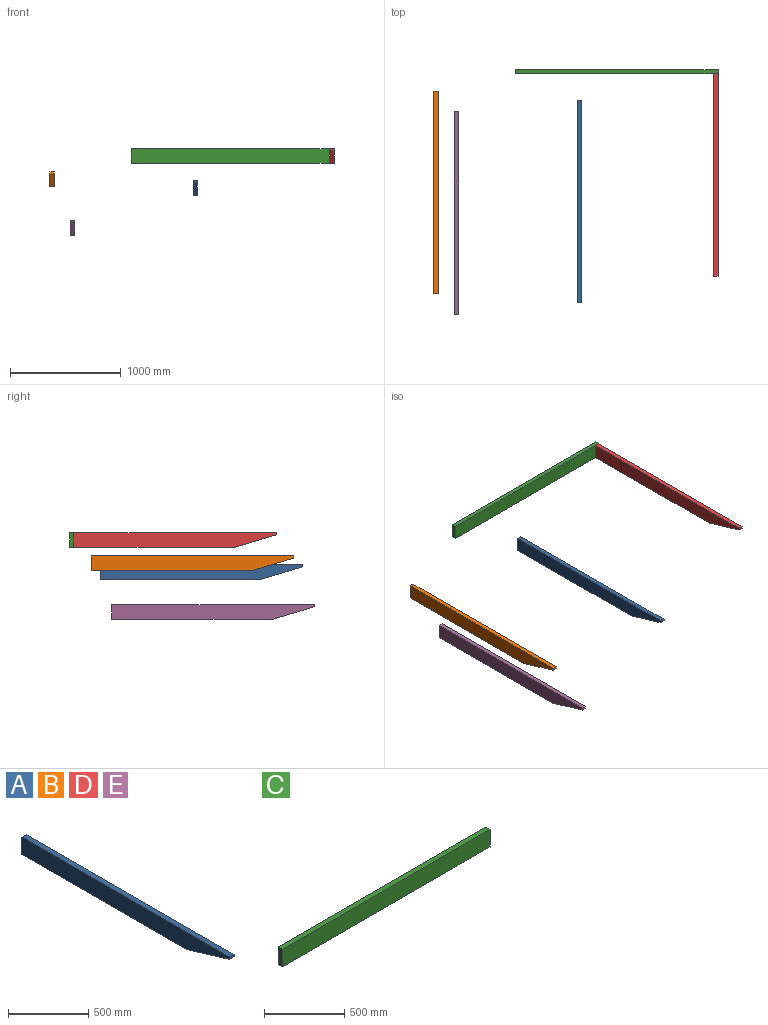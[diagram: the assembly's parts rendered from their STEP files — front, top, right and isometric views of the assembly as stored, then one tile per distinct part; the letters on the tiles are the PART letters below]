
ASSEMBLY  parts=5 mates=1
PART A: 7 faces, bbox 38.1x1828.8x133.4 mm
  f0: plane 1447.8x38.1mm, normal (0,0,-1), area 55161.2mm2, adj f2,f3,f5,f6
  f1: plane 38.1x19.05mm, normal (0,-1,0), area 725.8mm2, adj f2,f3,f4,f6
  f2: plane 1828.8x133.35mm, normal (-1,0,0), area 222096.3mm2, adj f0,f1,f4,f5,f6
  f3: plane 1828.8x133.35mm, normal (1,0,0), area 222096.3mm2, adj f0,f1,f4,f5,f6
  f4: plane 1828.8x38.1mm, normal (0,0,1), area 69677.3mm2, adj f1,f2,f3,f5
  f5: plane 133.35x38.1mm, normal (0,1,0), area 5080.6mm2, adj f0,f2,f3,f4
  f6: plane 381x114.3mm, normal (0,-0.29,-0.96), area 15155.3mm2, adj f0,f1,f2,f3
PART B: same geometry as A
PART C: 6 faces, bbox 1828.8x38.1x133.4 mm
  f0: plane 1828.8x133.35mm, normal (0,-1,0), area 243870.5mm2, adj f1,f3,f4,f5
  f1: plane 1828.8x38.1mm, normal (0,0,-1), area 69677.3mm2, adj f0,f2,f4,f5
  f2: plane 1828.8x133.35mm, normal (0,1,0), area 243870.5mm2, adj f1,f3,f4,f5
  f3: plane 1828.8x38.1mm, normal (0,0,1), area 69677.3mm2, adj f0,f2,f4,f5
  f4: plane 133.35x38.1mm, normal (1,0,0), area 5080.6mm2, adj f0,f1,f2,f3
  f5: plane 133.35x38.1mm, normal (-1,0,0), area 5080.6mm2, adj f0,f1,f2,f3
PART D: same geometry as A
PART E: same geometry as A
PLACE A t=(-308.34,-192.52,-297.41)mm
PLACE B t=(-1599.71,-110.55,-218.7)mm
PLACE C t=(29.34,45.86,-8.2)mm fixed
PLACE D t=(924.69,45.86,-8.2)mm
PLACE E t=(-1414.54,-295.78,-656.92)mm
MATE fastened D.f0 <-> C.f1  axis (0,0,1) through (943.74,45.86,-8.2)mm
